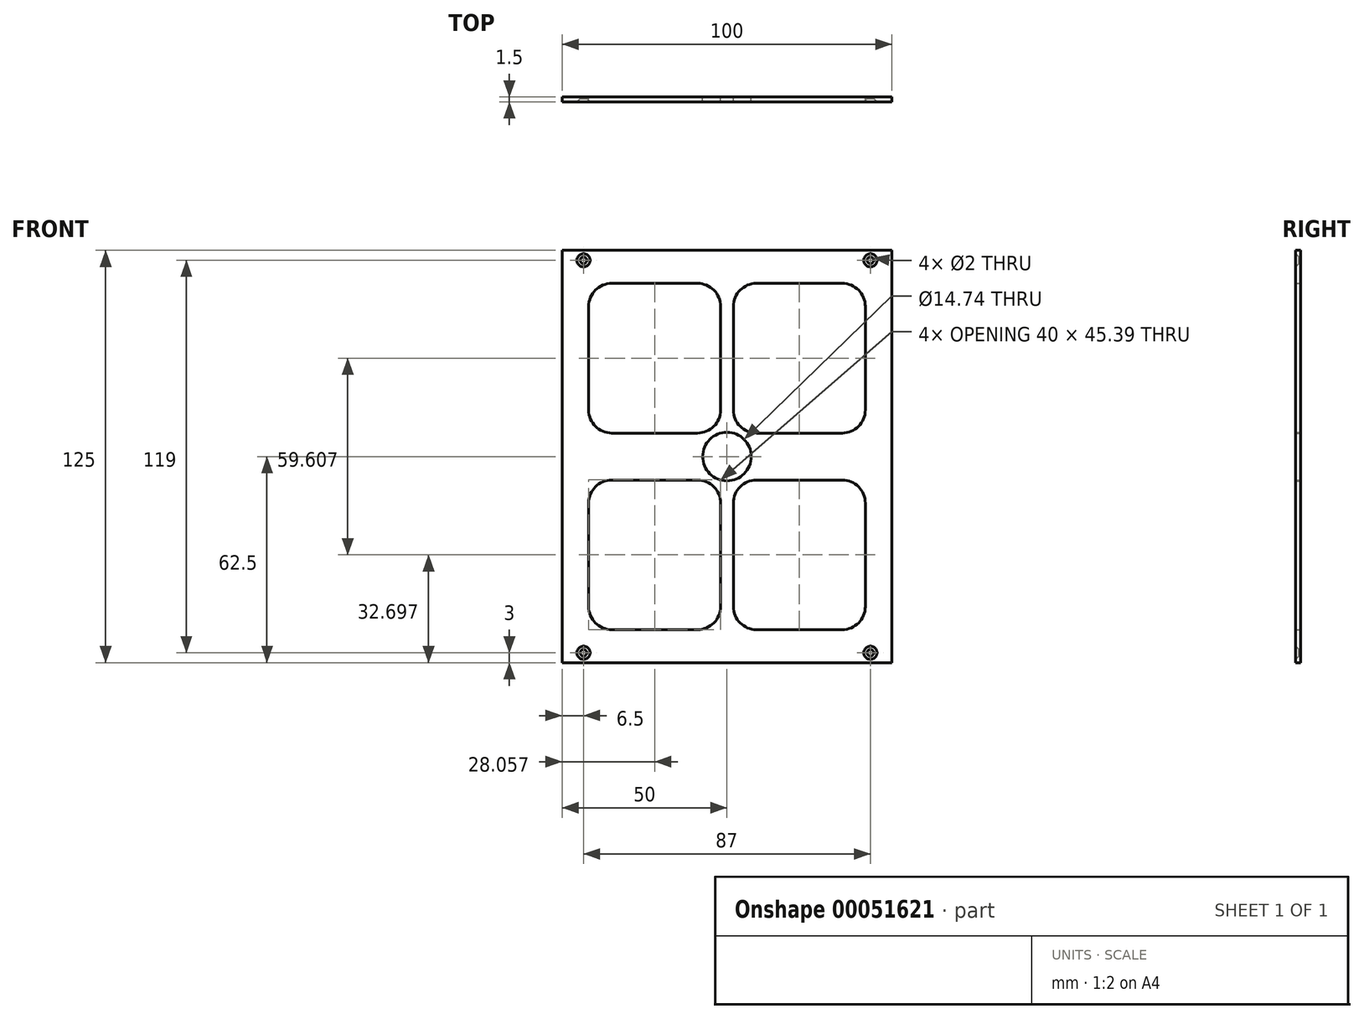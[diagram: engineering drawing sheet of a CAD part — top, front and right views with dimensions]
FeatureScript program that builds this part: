
annotation { "Feature Type Name" : "Feature", "Feature Type Description" : "" }
export const myFeature = defineFeature(function(context is Context, id is Id, definition is map)
    precondition{}
    {
        {
            var Q0;
            Q0=qCreatedBy(makeId("Front.planeOp"),FACE);
            var sketch = newSketch(context, id + "F0", { "sketchPlane" : qUnion([Q0])});
            skLineSegment(sketch, "E0.rect.bottom", {"start": v(-50, 62.5) * mm, "end": v(50, 62.5) * mm});
            skLineSegment(sketch, "E0.rect.top", {"start": v(-50, -62.5) * mm, "end": v(50, -62.5) * mm});
            skLineSegment(sketch, "E0.rect.left", {"start": v(-50, 62.5) * mm, "end": v(-50, -62.5) * mm});
            skLineSegment(sketch, "E0.rect.right", {"start": v(50, 62.5) * mm, "end": v(50, -62.5) * mm});
            skPoint(sketch, "E0.rect.middle", {"position": v(0, 0) * mm});
            skLineSegment(sketch, "E1.rect.bottom", {"start": v(-8.94, 7.1) * mm, "end": v(-34.94, 7.1) * mm});
            skLineSegment(sketch, "E1.rect.top", {"start": v(-8.94, 52.5) * mm, "end": v(-34.94, 52.5) * mm});
            skLineSegment(sketch, "E1.rect.left", {"start": v(-1.94, 14.1) * mm, "end": v(-1.94, 45.5) * mm});
            skLineSegment(sketch, "E1.rect.right", {"start": v(-41.94, 14.1) * mm, "end": v(-41.94, 45.5) * mm});
            skPoint(sketch, "E1.rect.middle", {"position": v(-21.94, 29.8) * mm});
            skPoint(sketch, "E2", {"position": v(0, 62.5) * mm});
            skPoint(sketch, "E3", {"position": v(-25, 62.5) * mm});
            skPoint(sketch, "E4.MirrorP", {"position": v(-25, -62.5) * mm});
            skPoint(sketch, "E5.visualSharp", {"position": v(-1.94, 7.1) * mm});
            skArc(sketch, "E5.filletArc", {"start": v(-8.94, 7.1) * mm, "mid": v(-4, 9.16) * mm, "end": v(-1.94, 14.1) * mm});
            skPoint(sketch, "E6.visualSharp", {"position": v(-1.94, 52.5) * mm});
            skArc(sketch, "E6.filletArc", {"start": v(-1.94, 45.5) * mm, "mid": v(-4, 50.45) * mm, "end": v(-8.94, 52.5) * mm});
            skPoint(sketch, "E7.visualSharp", {"position": v(-41.94, 52.5) * mm});
            skArc(sketch, "E7.filletArc", {"start": v(-34.94, 52.5) * mm, "mid": v(-39.9, 50.45) * mm, "end": v(-41.94, 45.5) * mm});
            skPoint(sketch, "E8.visualSharp", {"position": v(-41.94, 7.1) * mm});
            skArc(sketch, "E8.filletArc", {"start": v(-41.94, 14.1) * mm, "mid": v(-39.9, 9.16) * mm, "end": v(-34.94, 7.1) * mm});
            skLineSegment(sketch, "E9.MirrorCS", {"start": v(1.94, 14.1) * mm, "end": v(1.94, 45.5) * mm});
            skArc(sketch, "E10.MirrorCS", {"start": v(1.94, 45.5) * mm, "mid": v(4, 50.45) * mm, "end": v(8.94, 52.5) * mm});
            skLineSegment(sketch, "E11.MirrorCS", {"start": v(8.94, 52.5) * mm, "end": v(34.94, 52.5) * mm});
            skPoint(sketch, "E12.MirrorP", {"position": v(41.94, 52.5) * mm});
            skArc(sketch, "E13.MirrorCS", {"start": v(34.94, 52.5) * mm, "mid": v(39.9, 50.45) * mm, "end": v(41.94, 45.5) * mm});
            skLineSegment(sketch, "E14.MirrorCS", {"start": v(41.94, 14.1) * mm, "end": v(41.94, 45.5) * mm});
            skPoint(sketch, "E15.MirrorP", {"position": v(41.94, 7.1) * mm});
            skLineSegment(sketch, "E16.MirrorCS", {"start": v(8.94, 7.1) * mm, "end": v(34.94, 7.1) * mm});
            skArc(sketch, "E17.MirrorCS", {"start": v(41.94, 14.1) * mm, "mid": v(39.9, 9.16) * mm, "end": v(34.94, 7.1) * mm});
            skPoint(sketch, "E18.MirrorP", {"position": v(1.94, 7.1) * mm});
            skArc(sketch, "E19.MirrorCS", {"start": v(8.94, 7.1) * mm, "mid": v(4, 9.16) * mm, "end": v(1.94, 14.1) * mm});
            skPoint(sketch, "E20.MirrorP", {"position": v(1.94, 52.5) * mm});
            skArc(sketch, "E21.MirrorCS", {"start": v(34.94, -52.5) * mm, "mid": v(39.9, -50.45) * mm, "end": v(41.94, -45.5) * mm});
            skArc(sketch, "E22.MirrorCS", {"start": v(41.94, -14.1) * mm, "mid": v(39.9, -9.16) * mm, "end": v(34.94, -7.1) * mm});
            skArc(sketch, "E23.MirrorCS", {"start": v(8.94, -7.1) * mm, "mid": v(4, -9.16) * mm, "end": v(1.94, -14.1) * mm});
            skArc(sketch, "E24.MirrorCS", {"start": v(1.94, -45.5) * mm, "mid": v(4, -50.45) * mm, "end": v(8.94, -52.5) * mm});
            skPoint(sketch, "E25.MirrorP", {"position": v(41.94, -52.5) * mm});
            skLineSegment(sketch, "E26.MirrorCS", {"start": v(41.94, -14.1) * mm, "end": v(41.94, -45.5) * mm});
            skPoint(sketch, "E27.MirrorP", {"position": v(41.94, -7.1) * mm});
            skLineSegment(sketch, "E28.MirrorCS", {"start": v(1.94, -14.1) * mm, "end": v(1.94, -45.5) * mm});
            skPoint(sketch, "E29.MirrorP", {"position": v(1.94, -52.5) * mm});
            skLineSegment(sketch, "E30.MirrorCS", {"start": v(8.94, -7.1) * mm, "end": v(34.94, -7.1) * mm});
            skLineSegment(sketch, "E31.MirrorCS", {"start": v(8.94, -52.5) * mm, "end": v(34.94, -52.5) * mm});
            skPoint(sketch, "E32.MirrorP", {"position": v(1.94, -7.1) * mm});
            skArc(sketch, "E33.MirrorCS", {"start": v(-8.94, -7.1) * mm, "mid": v(-4, -9.16) * mm, "end": v(-1.94, -14.1) * mm});
            skArc(sketch, "E34.MirrorCS", {"start": v(-1.94, -45.5) * mm, "mid": v(-4, -50.45) * mm, "end": v(-8.94, -52.5) * mm});
            skArc(sketch, "E35.MirrorCS", {"start": v(-41.94, -14.1) * mm, "mid": v(-39.9, -9.16) * mm, "end": v(-34.94, -7.1) * mm});
            skArc(sketch, "E36.MirrorCS", {"start": v(-34.94, -52.5) * mm, "mid": v(-39.9, -50.45) * mm, "end": v(-41.94, -45.5) * mm});
            skPoint(sketch, "E37.MirrorP", {"position": v(-21.94, -29.8) * mm});
            skPoint(sketch, "E38.MirrorP", {"position": v(-1.94, -7.1) * mm});
            skPoint(sketch, "E39.MirrorP", {"position": v(-41.94, -52.5) * mm});
            skLineSegment(sketch, "E40.MirrorCS", {"start": v(-8.94, -7.1) * mm, "end": v(-34.94, -7.1) * mm});
            skLineSegment(sketch, "E41.MirrorCS", {"start": v(-8.94, -52.5) * mm, "end": v(-34.94, -52.5) * mm});
            skPoint(sketch, "E42.MirrorP", {"position": v(-1.94, -52.5) * mm});
            skLineSegment(sketch, "E43.MirrorCS", {"start": v(-1.94, -14.1) * mm, "end": v(-1.94, -45.5) * mm});
            skLineSegment(sketch, "E44.MirrorCS", {"start": v(-41.94, -14.1) * mm, "end": v(-41.94, -45.5) * mm});
            skPoint(sketch, "E45.MirrorP", {"position": v(-41.94, -7.1) * mm});
            skCircle(sketch, "E46", {"center": v(0, 0) * mm, "radius": 7.37 * mm});
            skSolve(sketch);
        }
        {
            var Q0;
            Q0=makeQuery(id+"F0.imprint","IMPRINT",FACE,{"disambiguationData":[TD([[makeQuery(id+"F0.imprint","IMPRINT",EDGE,{"derivedFrom":sQuery(id+"F0.wireOp",EDGE,"E0.rect.bottom")}),-1.0]])]});
            extrude(context, id + "F1", {"entities" : qUnion([Q0]), "depth" : 1.5 * mm});
        }
        {
            var Q0;
            Q0=makeQuery(id+"F1.opExtrude","CAP_FACE",FACE,{"disambiguationData":[OSD([sQuery(id+"F0.wireOp",EDGE,"E0.rect.bottom"),sQuery(id+"F0.wireOp",EDGE,"E0.rect.top"),sQuery(id+"F0.wireOp",EDGE,"E0.rect.left"),sQuery(id+"F0.wireOp",EDGE,"E0.rect.right"),sQuery(id+"F0.wireOp",EDGE,"E1.rect.bottom"),sQuery(id+"F0.wireOp",EDGE,"E1.rect.top"),sQuery(id+"F0.wireOp",EDGE,"E1.rect.left"),sQuery(id+"F0.wireOp",EDGE,"E1.rect.right"),sQuery(id+"F0.wireOp",EDGE,"E5.filletArc"),sQuery(id+"F0.wireOp",EDGE,"E6.filletArc"),sQuery(id+"F0.wireOp",EDGE,"E7.filletArc"),sQuery(id+"F0.wireOp",EDGE,"E8.filletArc"),sQuery(id+"F0.wireOp",EDGE,"E9.MirrorCS"),sQuery(id+"F0.wireOp",EDGE,"E10.MirrorCS"),sQuery(id+"F0.wireOp",EDGE,"E11.MirrorCS"),sQuery(id+"F0.wireOp",EDGE,"E13.MirrorCS"),sQuery(id+"F0.wireOp",EDGE,"E14.MirrorCS"),sQuery(id+"F0.wireOp",EDGE,"E16.MirrorCS"),sQuery(id+"F0.wireOp",EDGE,"E17.MirrorCS"),sQuery(id+"F0.wireOp",EDGE,"E19.MirrorCS"),sQuery(id+"F0.wireOp",EDGE,"E21.MirrorCS"),sQuery(id+"F0.wireOp",EDGE,"E22.MirrorCS"),sQuery(id+"F0.wireOp",EDGE,"E23.MirrorCS"),sQuery(id+"F0.wireOp",EDGE,"E24.MirrorCS"),sQuery(id+"F0.wireOp",EDGE,"E26.MirrorCS"),sQuery(id+"F0.wireOp",EDGE,"E28.MirrorCS"),sQuery(id+"F0.wireOp",EDGE,"E30.MirrorCS"),sQuery(id+"F0.wireOp",EDGE,"E31.MirrorCS"),sQuery(id+"F0.wireOp",EDGE,"E33.MirrorCS"),sQuery(id+"F0.wireOp",EDGE,"E34.MirrorCS"),sQuery(id+"F0.wireOp",EDGE,"E35.MirrorCS"),sQuery(id+"F0.wireOp",EDGE,"E36.MirrorCS"),sQuery(id+"F0.wireOp",EDGE,"E40.MirrorCS"),sQuery(id+"F0.wireOp",EDGE,"E41.MirrorCS"),sQuery(id+"F0.wireOp",EDGE,"E43.MirrorCS"),sQuery(id+"F0.wireOp",EDGE,"E44.MirrorCS"),sQuery(id+"F0.wireOp",EDGE,"deea28ce-c4f6-4fc3-8f0f-82602a925565.rect.bottom"),sQuery(id+"F0.wireOp",EDGE,"deea28ce-c4f6-4fc3-8f0f-82602a925565.rect.top"),sQuery(id+"F0.wireOp",EDGE,"deea28ce-c4f6-4fc3-8f0f-82602a925565.rect.left"),sQuery(id+"F0.wireOp",EDGE,"deea28ce-c4f6-4fc3-8f0f-82602a925565.rect.right"),sQuery(id+"F0.wireOp",EDGE,"92293470-82ba-44ad-9286-e8a1911384cd.filletArc"),sQuery(id+"F0.wireOp",EDGE,"f783d059-47c1-4597-a3b5-ce5ed20d1783.filletArc"),sQuery(id+"F0.wireOp",EDGE,"7d8a2005-66fb-4448-9a0b-17e6f11710ed.filletArc"),sQuery(id+"F0.wireOp",EDGE,"bd1f88c4-01d0-4c1f-b818-689555ed0d3d.filletArc"),sQuery(id+"F0.wireOp",EDGE,"3de75153-5ae1-45d4-89d9-6fcf70203f930.MirrorCS"),sQuery(id+"F0.wireOp",EDGE,"3de75153-5ae1-45d4-89d9-6fcf70203f931.MirrorCS"),sQuery(id+"F0.wireOp",EDGE,"3de75153-5ae1-45d4-89d9-6fcf70203f932.MirrorCS"),sQuery(id+"F0.wireOp",EDGE,"3de75153-5ae1-45d4-89d9-6fcf70203f933.MirrorCS"),sQuery(id+"F0.wireOp",EDGE,"3de75153-5ae1-45d4-89d9-6fcf70203f937.MirrorCS"),sQuery(id+"F0.wireOp",EDGE,"3de75153-5ae1-45d4-89d9-6fcf70203f939.MirrorCS"),sQuery(id+"F0.wireOp",EDGE,"3de75153-5ae1-45d4-89d9-6fcf70203f9311.MirrorCS"),sQuery(id+"F0.wireOp",EDGE,"3de75153-5ae1-45d4-89d9-6fcf70203f9312.MirrorCS")])],"isStart":false});
            var sketch = newSketch(context, id + "F2", { "sketchPlane" : qUnion([Q0])});
            skPoint(sketch, "E47", {"position": v(-43.5, -59.5) * mm});
            skPoint(sketch, "E48.MirrorP", {"position": v(43.5, -59.5) * mm});
            skPoint(sketch, "E49.MirrorP", {"position": v(-43.5, 59.5) * mm});
            skPoint(sketch, "E50.MirrorP", {"position": v(43.5, 59.5) * mm});
            skSolve(sketch);
        }
        {
            var Q0;
            Q0=sQuery(id+"F2.wireOp",VERTEX,"E47");
            var Q1;
            Q1=sQuery(id+"F2.wireOp",VERTEX,"E48.MirrorP");
            var Q2;
            Q2=sQuery(id+"F2.wireOp",VERTEX,"E50.MirrorP");
            var Q3;
            Q3=sQuery(id+"F2.wireOp",VERTEX,"E49.MirrorP");
            var Q4;
            Q4=sQuery(id+"F2.wireOp",VERTEX,"f692f96d-b3ef-4b25-bd05-95c4abe1053b");
            var Q5;
            Q5=sQuery(id+"F2.wireOp",VERTEX,"6fb1c37c-decf-44f5-8bba-7a2e60b1c09a");
            var Q6;
            Q6=sQuery(id+"F2.wireOp",VERTEX,"e5432b45-bd6c-42e0-96c4-d4a1cdefc3be");
            var Q7;
            Q7=sQuery(id+"F2.wireOp",VERTEX,"cf76a1ca-a373-4096-b586-4708a9325641");
            var Q8;
            Q8=sQuery(id+"F2.wireOp",VERTEX,"19e9ac87-c4db-4f84-8793-d0dcfe6b89480.MirrorP");
            var Q9;
            Q9=sQuery(id+"F2.wireOp",VERTEX,"cf40c92d-3cb4-4fd1-9011-2b1b11cf86800.MirrorP");
            var Q10;
            Q10=sQuery(id+"F2.wireOp",VERTEX,"dbe2afd2-cc13-4726-9d4e-a7426feb8f1a0.MirrorP");
            var Q11;
            Q11=sQuery(id+"F2.wireOp",VERTEX,"da7565b5-0760-4871-9ab9-0602c46f39720.MirrorP");
            var Q12;
            Q12=sQuery(id+"F2.wireOp",VERTEX,"17fecccd-3962-452f-9978-7328e825eee30.MirrorP");
            var Q13;
            Q13=sQuery(id+"F2.wireOp",VERTEX,"4bd07c42-14cb-4c0a-9484-79320a5c3db60.MirrorP");
            var Q14;
            Q14=sQuery(id+"F2.wireOp",VERTEX,"4bebc43e-6cee-4dba-a944-25e79cf908630.MirrorP");
            var Q15;
            Q15=sQuery(id+"F2.wireOp",VERTEX,"e56d2771-9223-44ee-8796-3a5c91e851be0.MirrorP");
            var Q16;
            Q16=sQuery(id+"F2.wireOp",VERTEX,"fc323023-5ca8-47af-bc60-2d4e8e6fe2a30.MirrorP");
            var Q17;
            Q17=sQuery(id+"F2.wireOp",VERTEX,"0839c29d-2d7f-409f-b01c-e3268e62f07b0.MirrorP");
            var Q18;
            Q18=sQuery(id+"F2.wireOp",VERTEX,"a23aa490-2248-47f4-872f-093390e742580.MirrorP");
            var Q19;
            Q19=sQuery(id+"F2.wireOp",VERTEX,"f29489ae-a8f8-488d-b8ee-71de4e1048c30.MirrorP");
            var Q20;
            Q20=makeQuery(id+"F1.opExtrude","SWEPT_BODY",BODY,{"disambiguationData":[OSD([sQuery(id+"F0.wireOp",EDGE,"E0.rect.bottom"),sQuery(id+"F0.wireOp",EDGE,"E0.rect.top"),sQuery(id+"F0.wireOp",EDGE,"E0.rect.left"),sQuery(id+"F0.wireOp",EDGE,"E0.rect.right"),sQuery(id+"F0.wireOp",EDGE,"E1.rect.bottom"),sQuery(id+"F0.wireOp",EDGE,"E1.rect.top"),sQuery(id+"F0.wireOp",EDGE,"E1.rect.left"),sQuery(id+"F0.wireOp",EDGE,"E1.rect.right"),sQuery(id+"F0.wireOp",EDGE,"E5.filletArc"),sQuery(id+"F0.wireOp",EDGE,"E6.filletArc"),sQuery(id+"F0.wireOp",EDGE,"E7.filletArc"),sQuery(id+"F0.wireOp",EDGE,"E8.filletArc"),sQuery(id+"F0.wireOp",EDGE,"E9.MirrorCS"),sQuery(id+"F0.wireOp",EDGE,"E10.MirrorCS"),sQuery(id+"F0.wireOp",EDGE,"E11.MirrorCS"),sQuery(id+"F0.wireOp",EDGE,"E13.MirrorCS"),sQuery(id+"F0.wireOp",EDGE,"E14.MirrorCS"),sQuery(id+"F0.wireOp",EDGE,"E16.MirrorCS"),sQuery(id+"F0.wireOp",EDGE,"E17.MirrorCS"),sQuery(id+"F0.wireOp",EDGE,"E19.MirrorCS"),sQuery(id+"F0.wireOp",EDGE,"E21.MirrorCS"),sQuery(id+"F0.wireOp",EDGE,"E22.MirrorCS"),sQuery(id+"F0.wireOp",EDGE,"E23.MirrorCS"),sQuery(id+"F0.wireOp",EDGE,"E24.MirrorCS"),sQuery(id+"F0.wireOp",EDGE,"E26.MirrorCS"),sQuery(id+"F0.wireOp",EDGE,"E28.MirrorCS"),sQuery(id+"F0.wireOp",EDGE,"E30.MirrorCS"),sQuery(id+"F0.wireOp",EDGE,"E31.MirrorCS"),sQuery(id+"F0.wireOp",EDGE,"E33.MirrorCS"),sQuery(id+"F0.wireOp",EDGE,"E34.MirrorCS"),sQuery(id+"F0.wireOp",EDGE,"E35.MirrorCS"),sQuery(id+"F0.wireOp",EDGE,"E36.MirrorCS"),sQuery(id+"F0.wireOp",EDGE,"E40.MirrorCS"),sQuery(id+"F0.wireOp",EDGE,"E41.MirrorCS"),sQuery(id+"F0.wireOp",EDGE,"E43.MirrorCS"),sQuery(id+"F0.wireOp",EDGE,"E44.MirrorCS"),sQuery(id+"F0.wireOp",EDGE,"deea28ce-c4f6-4fc3-8f0f-82602a925565.rect.bottom"),sQuery(id+"F0.wireOp",EDGE,"deea28ce-c4f6-4fc3-8f0f-82602a925565.rect.top"),sQuery(id+"F0.wireOp",EDGE,"deea28ce-c4f6-4fc3-8f0f-82602a925565.rect.left"),sQuery(id+"F0.wireOp",EDGE,"deea28ce-c4f6-4fc3-8f0f-82602a925565.rect.right"),sQuery(id+"F0.wireOp",EDGE,"92293470-82ba-44ad-9286-e8a1911384cd.filletArc"),sQuery(id+"F0.wireOp",EDGE,"f783d059-47c1-4597-a3b5-ce5ed20d1783.filletArc"),sQuery(id+"F0.wireOp",EDGE,"7d8a2005-66fb-4448-9a0b-17e6f11710ed.filletArc"),sQuery(id+"F0.wireOp",EDGE,"bd1f88c4-01d0-4c1f-b818-689555ed0d3d.filletArc"),sQuery(id+"F0.wireOp",EDGE,"3de75153-5ae1-45d4-89d9-6fcf70203f930.MirrorCS"),sQuery(id+"F0.wireOp",EDGE,"3de75153-5ae1-45d4-89d9-6fcf70203f931.MirrorCS"),sQuery(id+"F0.wireOp",EDGE,"3de75153-5ae1-45d4-89d9-6fcf70203f932.MirrorCS"),sQuery(id+"F0.wireOp",EDGE,"3de75153-5ae1-45d4-89d9-6fcf70203f933.MirrorCS"),sQuery(id+"F0.wireOp",EDGE,"3de75153-5ae1-45d4-89d9-6fcf70203f937.MirrorCS"),sQuery(id+"F0.wireOp",EDGE,"3de75153-5ae1-45d4-89d9-6fcf70203f939.MirrorCS"),sQuery(id+"F0.wireOp",EDGE,"3de75153-5ae1-45d4-89d9-6fcf70203f9311.MirrorCS"),sQuery(id+"F0.wireOp",EDGE,"3de75153-5ae1-45d4-89d9-6fcf70203f9312.MirrorCS")])]});
            hole(context, id + "F3", {"style" : HoleStyle.C_SINK, "holeDiameter" : 2 * mm, "cSinkDiameter" : 4 * mm, "endStyle" : HoleEndStyle.THROUGH, "locations" : qUnion([Q0, Q1, Q2, Q3, Q4, Q5, Q6, Q7, Q8, Q9, Q10, Q11, Q12, Q13, Q14, Q15, Q16, Q17, Q18, Q19]), "scope" : qUnion([Q20]), "cSinkAngle" : 90 * degree});
        }
    });
